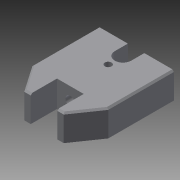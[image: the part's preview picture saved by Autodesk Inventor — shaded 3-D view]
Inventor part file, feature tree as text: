
AUTODESK INVENTOR PART (.ipt)
format: ipt  version: 2015 (Build 190159000, 159)  size: 147,968 bytes
history: native  units: in
note: dims shown in document units (in); Inventor stores cm internally (conversion verified against a paired STEP export)
features: sketch x6, extrude x4, hole x2, chamfer x1
ambient origin geometry x8: Origin, YZ Plane, XZ Plane, XY Plane, X Axis, Y Axis, Z Axis, Center Point
bodies: Solid1 (feature_tree)
feature tree (13):
  extrude  "Extrusion1"  Depth=3.5in
  extrude  "Extrusion2"  Depth=2.885in
  extrude  "Extrusion3"  Depth=0.313in
  extrude  "Extrusion4"  Depth=0.5in
  chamfer  "Chamfer1"  Distance=2.885in
  hole  "Hole1"  [1 undecoded]
  hole  "Hole2"  [1 undecoded]
  sketch  "Sketch1"  dims[d0=1.0in d1=3.5in]
  sketch  "Sketch2"  dims[d2=2.885in d3=0.0in d5=1.438in]
  sketch  "Sketch3"  dims[d6=0.313in d7=0.5in]
  sketch  "Sketch4"  dims[d8=0.0in d9=0.5in]
  sketch  "Sketch5"  dims[d10=0.5in d11=2.885in d12=0.0in]
  sketch  "Sketch6"  dims[d13=0.69in d14=0.69in d15=2.5in d16=2.5in d17=2.885in d18=0.0in d19=1.015in d20=0.938in d21=1.0in d22=0.0in d23=0.06in d24=0.125in d25=45.0deg d26=1.062in d27=1.438in d28=0.255in d29=0.75in d30=0.375in d31=0.25in d32=0.5635in d33=0.562in d34=0.8108in d35=0.5in d36=0.5075in d37=0.375in d38=0.75in d39=0.375in d40=0.25in d41=0.5635in d42=0.75in d43=0.8108in]
note: 2 required parameter values undecoded (feature->parameter linkage not recoverable at this tier; creation-order binding heuristic only, values carry confidence <= 0.55)
